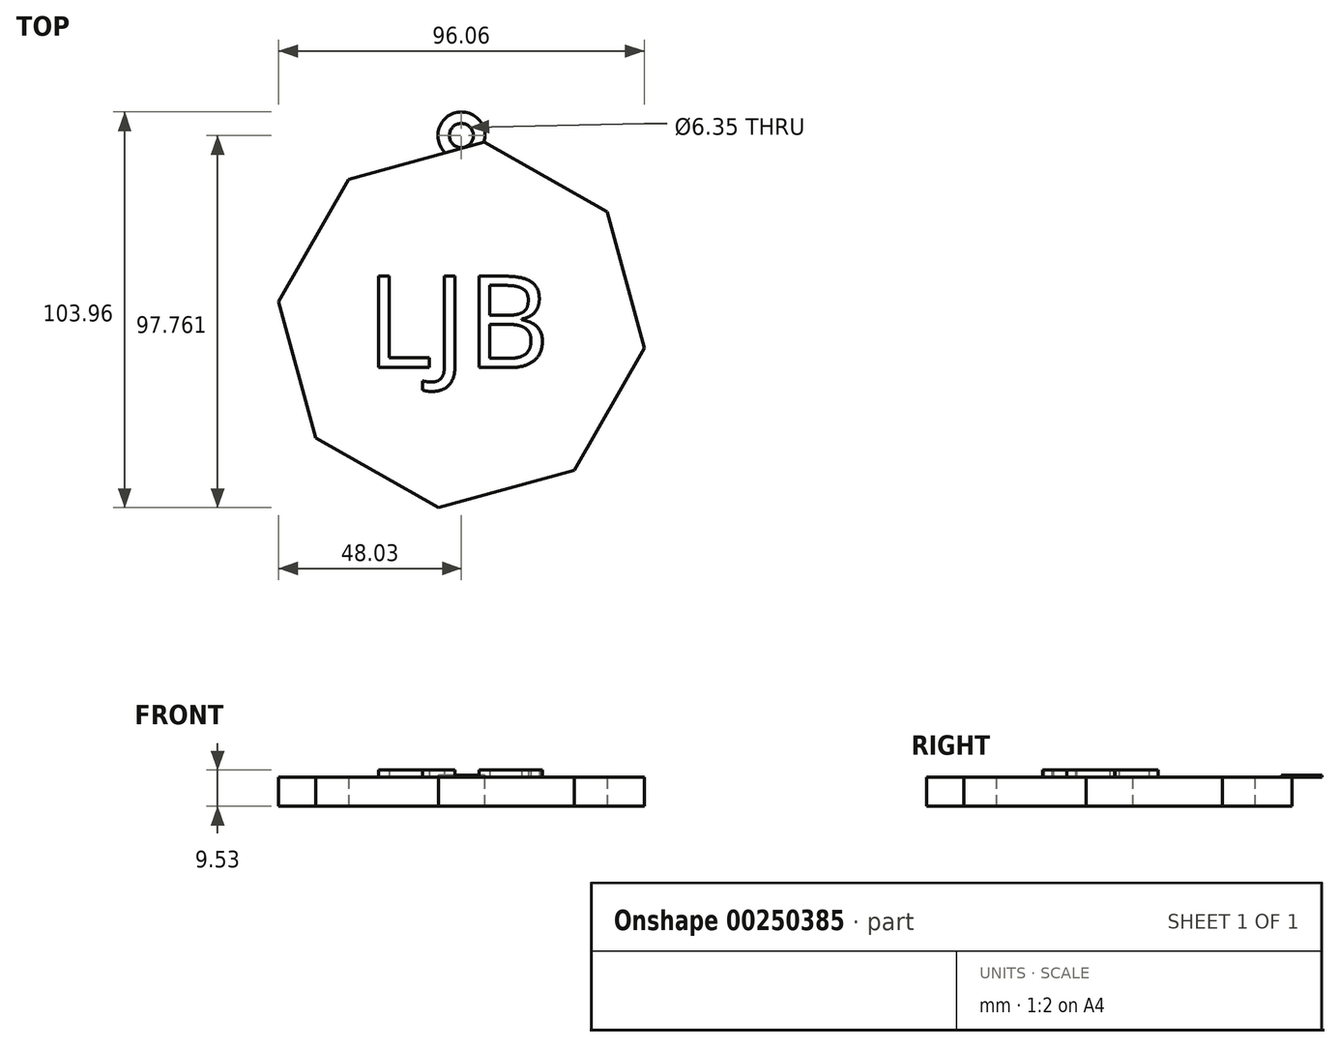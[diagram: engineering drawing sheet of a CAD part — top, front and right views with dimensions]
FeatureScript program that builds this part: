
annotation { "Feature Type Name" : "Feature", "Feature Type Description" : "" }
export const myFeature = defineFeature(function(context is Context, id is Id, definition is map)
    precondition{}
    {
        {
            var Q0;
            Q0=qCreatedBy(makeId("Top.planeOp"),FACE);
            var sketch = newSketch(context, id + "F0", { "sketchPlane" : qUnion([Q0])});
            skCircle(sketch, "E0.cCircle", {"center": v(0, 0) * mm, "radius": 44.73 * mm, "construction": true});
            skLineSegment(sketch, "E0.0", {"start": v(-6.07, -48.03) * mm, "end": v(-38.25, -29.67) * mm});
            skLineSegment(sketch, "E0.1", {"start": v(-38.25, -29.67) * mm, "end": v(-48.03, 6.07) * mm});
            skLineSegment(sketch, "E0.2", {"start": v(-48.03, 6.07) * mm, "end": v(-29.67, 38.25) * mm});
            skLineSegment(sketch, "E0.3", {"start": v(-29.67, 38.25) * mm, "end": v(6.07, 48.03) * mm});
            skLineSegment(sketch, "E0.4", {"start": v(6.07, 48.03) * mm, "end": v(38.25, 29.67) * mm});
            skLineSegment(sketch, "E0.5", {"start": v(38.25, 29.67) * mm, "end": v(48.03, -6.07) * mm});
            skLineSegment(sketch, "E0.6", {"start": v(48.03, -6.07) * mm, "end": v(29.67, -38.25) * mm});
            skLineSegment(sketch, "E0.7", {"start": v(29.67, -38.25) * mm, "end": v(-6.07, -48.03) * mm});
            skPoint(sketch, "E0.0.midPoint", {"position": v(-22.16, -38.85) * mm});
            skSolve(sketch);
        }
        {
            var Q0;
            Q0=makeQuery(id+"F0.imprint","IMPRINT",FACE,{"disambiguationData":[TD([[makeQuery(id+"F0.imprint","IMPRINT",EDGE,{"derivedFrom":sQuery(id+"F0.wireOp",EDGE,"E0.0")}),-1.0]])]});
            extrude(context, id + "F1", {"entities" : qUnion([Q0]), "depth" : 7.62 * mm});
        }
        {
            var Q0;
            Q0=makeQuery(id+"F1.opExtrude","CAP_FACE",FACE,{"disambiguationData":[OSD([sQuery(id+"F0.wireOp",EDGE,"E0.0"),sQuery(id+"F0.wireOp",EDGE,"E0.1"),sQuery(id+"F0.wireOp",EDGE,"E0.2"),sQuery(id+"F0.wireOp",EDGE,"E0.3"),sQuery(id+"F0.wireOp",EDGE,"E0.4"),sQuery(id+"F0.wireOp",EDGE,"E0.5"),sQuery(id+"F0.wireOp",EDGE,"E0.6"),sQuery(id+"F0.wireOp",EDGE,"E0.7")])],"isStart":false});
            var sketch = newSketch(context, id + "F2", { "sketchPlane" : qUnion([Q0])});
            skText(sketch, "E1", { "text": "LJB", "fontName": "OpenSans-Regular.ttf"});
            const initialGuessF2  = {"E1": [-0.02504, -0.01122, 1, 0, 0.02418]};
            skSetInitialGuess(sketch, initialGuessF2);
            skSolve(sketch);
        }
        {
            var Q0;
            Q0=makeQuery(id+"F2.imprint","IMPRINT",FACE,{"disambiguationData":[TD([[makeQuery(id+"F2.imprint","IMPRINT",EDGE,{"derivedFrom":sQuery(id+"F2.wireOp",EDGE,"E1.sketch_text.stroke-0")}),1.0]])]});
            var sketch = newSketch(context, id + "F3", { "sketchPlane" : qUnion([Q0])});
            skArc(sketch, "E2", {"start": v(-47.9, 6.08) * mm, "mid": v(-23, 13.07) * mm, "end": v(-29.93, 38) * mm});
            skArc(sketch, "E3", {"start": v(-38.19, -29.75) * mm, "mid": v(-25.24, -7) * mm, "end": v(-47.9, 6.08) * mm});
            skArc(sketch, "E4", {"start": v(-6.07, -48.08) * mm, "mid": v(-12.97, -22.87) * mm, "end": v(-38.19, -29.75) * mm});
            skArc(sketch, "E5", {"start": v(-29.93, 38) * mm, "mid": v(-6.96, 25.18) * mm, "end": v(6.1, 48.01) * mm});
            skArc(sketch, "E6", {"start": v(29.57, -38.43) * mm, "mid": v(6.92, -25.43) * mm, "end": v(-6.07, -48.08) * mm});
            skArc(sketch, "E7", {"start": v(47.96, -6.01) * mm, "mid": v(22.56, -13.03) * mm, "end": v(29.57, -38.43) * mm});
            skArc(sketch, "E8", {"start": v(37.84, 29.69) * mm, "mid": v(25.36, 6.87) * mm, "end": v(47.96, -6.01) * mm});
            skArc(sketch, "E9", {"start": v(6.1, 48.01) * mm, "mid": v(12.92, 23.18) * mm, "end": v(37.84, 29.69) * mm});
            skSolve(sketch);
        }
        {
            var Q0;
            Q0 = qSketchRegion(id + "F2", true);
            extrude(context, id + "F4", {"entities" : qUnion([Q0]), "operationType" : NewBodyOperationType.ADD, "depth" : 1.9 * mm});
        }
        {
            var Q0;
            {var subQ17=makeQuery(id+"F2.imprint","IMPRINT",EDGE,{"derivedFrom":makeQuery(id+"F1.opExtrude","CAP_EDGE",EDGE,{"disambiguationData":[OSD([sQuery(id+"F0.wireOp",EDGE,"E0.3")])],"isStart":false})});Q0=makeQuery(id+"F3.imprint","IMPRINT",FACE,{"disambiguationData":[TD([[makeQuery(id+"F3.imprint","IMPRINT",EDGE,{"derivedFrom":subQ17}),-1.0]])]});}
            var sketch = newSketch(context, id + "F5", { "sketchPlane" : qUnion([Q0])});
            skCircle(sketch, "E10", {"center": v(0, 49.73) * mm, "radius": 6.2 * mm});
            skSolve(sketch);
        }
        {
            var Q0;
            {var subQ0=sQuery(id+"F5.wireOp",EDGE,"E10");var subQ1=makeQuery(id+"F3.imprint","IMPRINT",EDGE,{"derivedFrom":makeQuery(id+"F2.imprint","IMPRINT",EDGE,{"derivedFrom":makeQuery(id+"F1.opExtrude","CAP_EDGE",EDGE,{"disambiguationData":[OSD([sQuery(id+"F0.wireOp",EDGE,"E0.3")])],"isStart":false})})});var subQ2=makeQuery(id+"F5.imprint","INTERSECT",VERTEX,{"disambiguationData":[OD(0.0)],"derivedFrom":[subQ1,subQ0]});Q0=makeQuery(id+"F5.imprint","IMPRINT",FACE,{"disambiguationData":[TD([[makeQuery(id+"F5.imprint","IMPRINT",EDGE,{"disambiguationData":[TD([[subQ2,1.0]])],"derivedFrom":subQ0}),1.0]])]});}
            var sketch = newSketch(context, id + "F6", { "sketchPlane" : qUnion([Q0])});
            skCircle(sketch, "E11", {"center": v(0, 49.73) * mm, "radius": 4.41 * mm});
            skSolve(sketch);
        }
        {
            var Q0;
            {var subQ0=sQuery(id+"F5.wireOp",EDGE,"E10");var subQ1=makeQuery(id+"F3.imprint","IMPRINT",EDGE,{"derivedFrom":makeQuery(id+"F2.imprint","IMPRINT",EDGE,{"derivedFrom":makeQuery(id+"F1.opExtrude","CAP_EDGE",EDGE,{"disambiguationData":[OSD([sQuery(id+"F0.wireOp",EDGE,"E0.3")])],"isStart":false})})});var subQ2=makeQuery(id+"F5.imprint","INTERSECT",VERTEX,{"disambiguationData":[OD(0.0)],"derivedFrom":[subQ1,subQ0]});Q0=makeQuery(id+"F5.imprint","IMPRINT",FACE,{"disambiguationData":[TD([[makeQuery(id+"F5.imprint","IMPRINT",EDGE,{"disambiguationData":[TD([[subQ2,1.0]])],"derivedFrom":subQ0}),1.0]])]});}
            extrude(context, id + "F7", {"entities" : qUnion([Q0]), "depth" : 0.5 * mm});
        }
        {
            var Q0;
            Q0=sQuery(id+"F6.wireOp",VERTEX,"E11.center");
            var Q1;
            Q1=makeQuery(id+"F7.opExtrude","SWEPT_BODY",BODY,{"disambiguationData":[OSD([sQuery(id+"F0.wireOp",EDGE,"E0.3"),sQuery(id+"F5.wireOp",EDGE,"E10")])]});
            hole(context, id + "F8", {"style" : HoleStyle.SIMPLE, "endStyle" : HoleEndStyle.THROUGH, "oppositeDirection" : true, "holeDiameter" : 6.35 * mm, "tappedDepth" : 12.7 * mm, "tapClearance" : 3, "locations" : qUnion([Q0]), "scope" : qUnion([Q1])});
        }
    });
